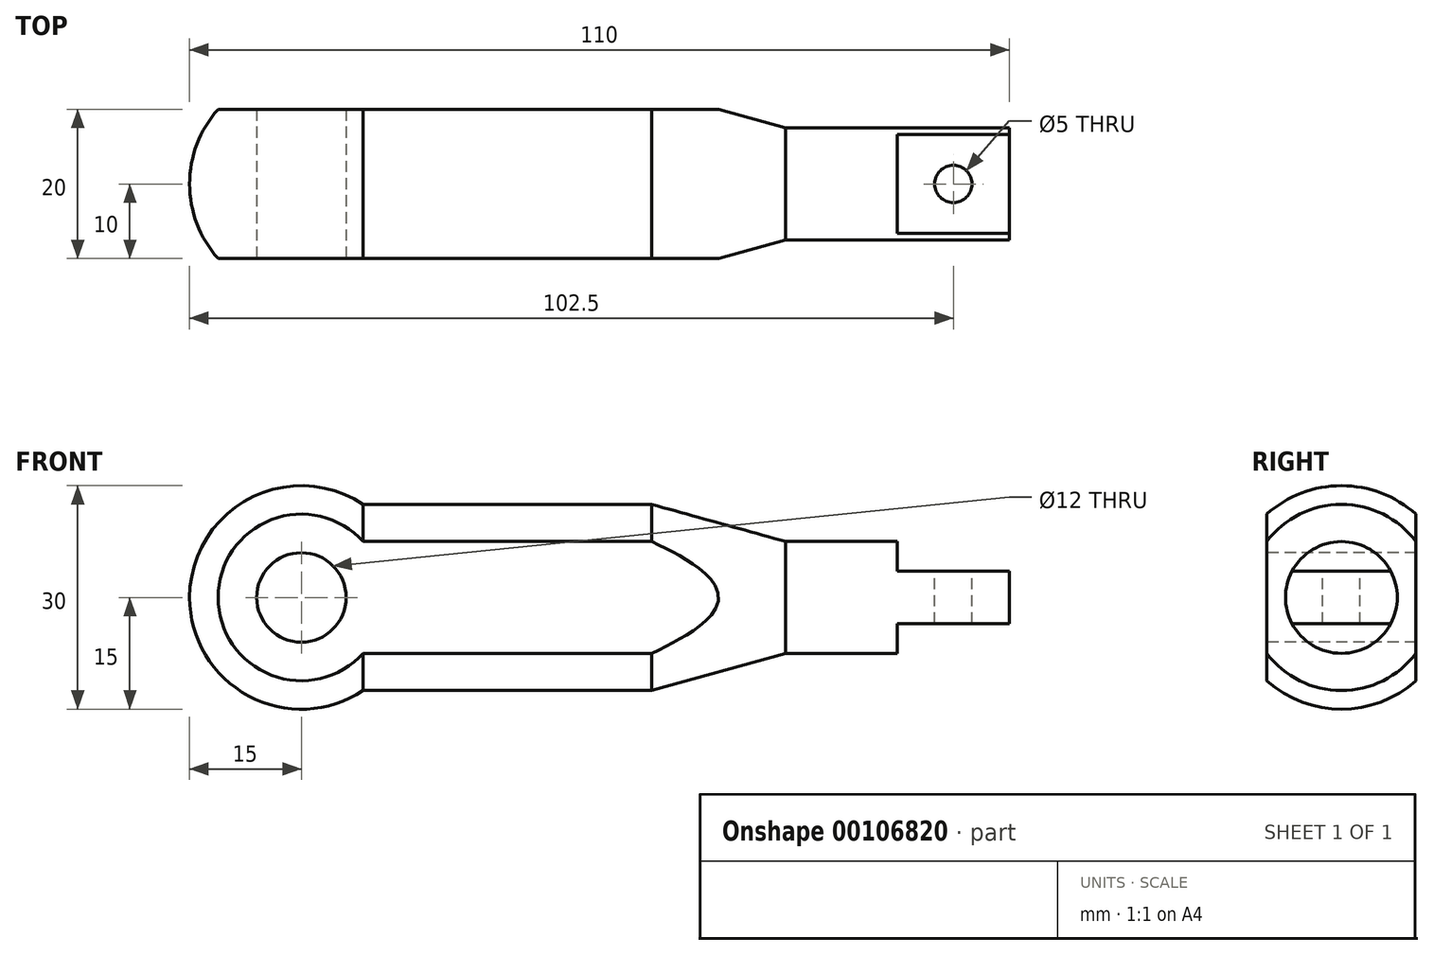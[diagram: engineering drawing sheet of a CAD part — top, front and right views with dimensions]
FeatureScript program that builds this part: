
annotation { "Feature Type Name" : "Feature", "Feature Type Description" : "" }
export const myFeature = defineFeature(function(context is Context, id is Id, definition is map)
    precondition{}
    {
        {
            var Q0;
            Q0=qCreatedBy(makeId("Front.planeOp"),FACE);
            var sketch = newSketch(context, id + "F0", { "sketchPlane" : qUnion([Q0])});
            skLineSegment(sketch, "E0", {"start": v(8.3, 12.5) * mm, "end": v(47, 12.5) * mm});
            skLineSegment(sketch, "E1", {"start": v(47, 12.5) * mm, "end": v(65, 7.5) * mm});
            skLineSegment(sketch, "E2", {"start": v(65, 7.5) * mm, "end": v(80, 7.5) * mm});
            skLineSegment(sketch, "E3", {"start": v(80, 7.5) * mm, "end": v(80, 7.5) * mm});
            skLineSegment(sketch, "E4", {"start": v(80, 7.5) * mm, "end": v(95, 7.5) * mm});
            skLineSegment(sketch, "E5", {"start": v(95, 7.5) * mm, "end": v(95, 0) * mm});
            skArc(sketch, "E6", {"start": v(-15, 0) * mm, "mid": v(-7.1, 13.22) * mm, "end": v(8.3, 12.5) * mm});
            skLineSegment(sketch, "E7", {"start": v(-15, 0) * mm, "end": v(95, 0) * mm});
            skSolve(sketch);
        }
        {
            var Q0;
            Q0=makeQuery(id+"F0.imprint","IMPRINT",FACE,{"disambiguationData":[TD([[makeQuery(id+"F0.imprint","IMPRINT",EDGE,{"derivedFrom":sQuery(id+"F0.wireOp",EDGE,"E0")}),-1.0]])]});
            var Q1;
            Q1=sQuery(id+"F0.wireOp",EDGE,"E6");
            var Q2;
            Q2=sQuery(id+"F0.wireOp",EDGE,"E0");
            var Q3;
            Q3=sQuery(id+"F0.wireOp",EDGE,"E1");
            var Q4;
            Q4=sQuery(id+"F0.wireOp",EDGE,"E2");
            var Q5;
            Q5=sQuery(id+"F0.wireOp",EDGE,"E4");
            var Q6;
            Q6=sQuery(id+"F0.wireOp",EDGE,"E3");
            var Q7;
            Q7=sQuery(id+"F0.wireOp",EDGE,"E5");
            var Q8;
            Q8=sQuery(id+"F0.wireOp",EDGE,"E7");
            revolve(context, id + "F1", {"entities" : qUnion([Q0]), "surfaceEntities" : qUnion([Q1, Q2, Q3, Q4, Q5, Q6, Q7]), "axis" : qUnion([Q8]), "revolveType" : RevolveType.FULL});
        }
        {
            var Q0;
            Q0=qCreatedBy(makeId("Front.planeOp"),FACE);
            var sketch = newSketch(context, id + "F2", { "sketchPlane" : qUnion([Q0])});
            skLineSegment(sketch, "E8.bottom", {"start": v(80, 7.5) * mm, "end": v(95, 7.5) * mm});
            skLineSegment(sketch, "E8.top", {"start": v(80, 3.5) * mm, "end": v(95, 3.5) * mm});
            skLineSegment(sketch, "E8.left", {"start": v(80, 7.5) * mm, "end": v(80, 3.5) * mm});
            skLineSegment(sketch, "E8.right", {"start": v(95, 7.5) * mm, "end": v(95, 3.5) * mm});
            skLineSegment(sketch, "E9.MirrorCS", {"start": v(80, -7.5) * mm, "end": v(95, -7.5) * mm});
            skLineSegment(sketch, "E10.MirrorCS", {"start": v(80, -7.5) * mm, "end": v(80, -3.5) * mm});
            skLineSegment(sketch, "E11.MirrorCS", {"start": v(80, -3.5) * mm, "end": v(95, -3.5) * mm});
            skLineSegment(sketch, "E12.MirrorCS", {"start": v(95, -7.5) * mm, "end": v(95, -3.5) * mm});
            skSolve(sketch);
        }
        {
            var Q0;
            Q0 = qSketchRegion(id + "F2", true);
            extrude(context, id + "F3", {"entities" : qUnion([Q0]), "operationType" : NewBodyOperationType.REMOVE, "endBound" : BoundingType.THROUGH_ALL, "oppositeDirection" : true, "depth" : 25 * mm, "hasSecondDirection" : true, "secondDirectionBound" : SecondDirectionBoundingType.THROUGH_ALL, "secondDirectionOppositeDirection" : false, "secondDirectionDepth" : 25 * mm});
        }
        {
            var Q0;
            Q0=makeQuery(id+"F3.boolean.opBoolean","COPY",FACE,{"derivedFrom":makeQuery(id+"F3.opExtrude","SWEPT_FACE",FACE,{"disambiguationData":[OSD([sQuery(id+"F2.wireOp",EDGE,"E8.top")])]})});
            var sketch = newSketch(context, id + "F4", { "sketchPlane" : qUnion([Q0])});
            skCircle(sketch, "E13", {"center": v(87.5, 0) * mm, "radius": 2.5 * mm});
            skSolve(sketch);
        }
        {
            var Q0;
            Q0=makeQuery(id+"F4.imprint","IMPRINT",FACE,{"disambiguationData":[TD([[makeQuery(id+"F4.imprint","IMPRINT",EDGE,{"derivedFrom":sQuery(id+"F4.wireOp",EDGE,"E13")}),1.0]])]});
            extrude(context, id + "F5", {"entities" : qUnion([Q0]), "operationType" : NewBodyOperationType.REMOVE, "endBound" : BoundingType.THROUGH_ALL, "oppositeDirection" : true, "depth" : 25 * mm});
        }
        {
            var Q0;
            Q0=qCreatedBy(makeId("Right.planeOp"),FACE);
            var sketch = newSketch(context, id + "F6", { "sketchPlane" : qUnion([Q0])});
            skLineSegment(sketch, "E14.bottom", {"start": v(-10, 18.22) * mm, "end": v(-22.33, 18.22) * mm});
            skLineSegment(sketch, "E14.top", {"start": v(-10, -17.9) * mm, "end": v(-22.33, -17.9) * mm});
            skLineSegment(sketch, "E14.left", {"start": v(-10, 18.22) * mm, "end": v(-10, -17.9) * mm});
            skLineSegment(sketch, "E14.right", {"start": v(-22.33, 18.22) * mm, "end": v(-22.33, -17.9) * mm});
            skLineSegment(sketch, "E15.MirrorCS", {"start": v(10, 18.22) * mm, "end": v(10, -17.9) * mm});
            skLineSegment(sketch, "E16.MirrorCS", {"start": v(10, 18.22) * mm, "end": v(22.33, 18.22) * mm});
            skLineSegment(sketch, "E17.MirrorCS", {"start": v(22.33, 18.22) * mm, "end": v(22.33, -17.9) * mm});
            skLineSegment(sketch, "E18.MirrorCS", {"start": v(10, -17.9) * mm, "end": v(22.33, -17.9) * mm});
            skSolve(sketch);
        }
        {
            var Q0;
            Q0 = qSketchRegion(id + "F6", true);
            extrude(context, id + "F7", {"entities" : qUnion([Q0]), "operationType" : NewBodyOperationType.REMOVE, "endBound" : BoundingType.THROUGH_ALL, "oppositeDirection" : true, "depth" : 25 * mm, "hasSecondDirection" : true, "secondDirectionBound" : SecondDirectionBoundingType.THROUGH_ALL, "secondDirectionOppositeDirection" : false, "secondDirectionDepth" : 25 * mm});
        }
        {
            var Q0;
            Q0=qCreatedBy(makeId("Front.planeOp"),FACE);
            var sketch = newSketch(context, id + "F8", { "sketchPlane" : qUnion([Q0])});
            skCircle(sketch, "E19", {"center": v(0, 0) * mm, "radius": 6 * mm});
            skSolve(sketch);
        }
        {
            var Q0;
            Q0 = qSketchRegion(id + "F8", true);
            extrude(context, id + "F9", {"entities" : qUnion([Q0]), "operationType" : NewBodyOperationType.REMOVE, "endBound" : BoundingType.THROUGH_ALL, "oppositeDirection" : true, "depth" : 25 * mm, "hasSecondDirection" : true, "secondDirectionBound" : SecondDirectionBoundingType.THROUGH_ALL, "secondDirectionOppositeDirection" : false, "secondDirectionDepth" : 25 * mm});
        }
    });
